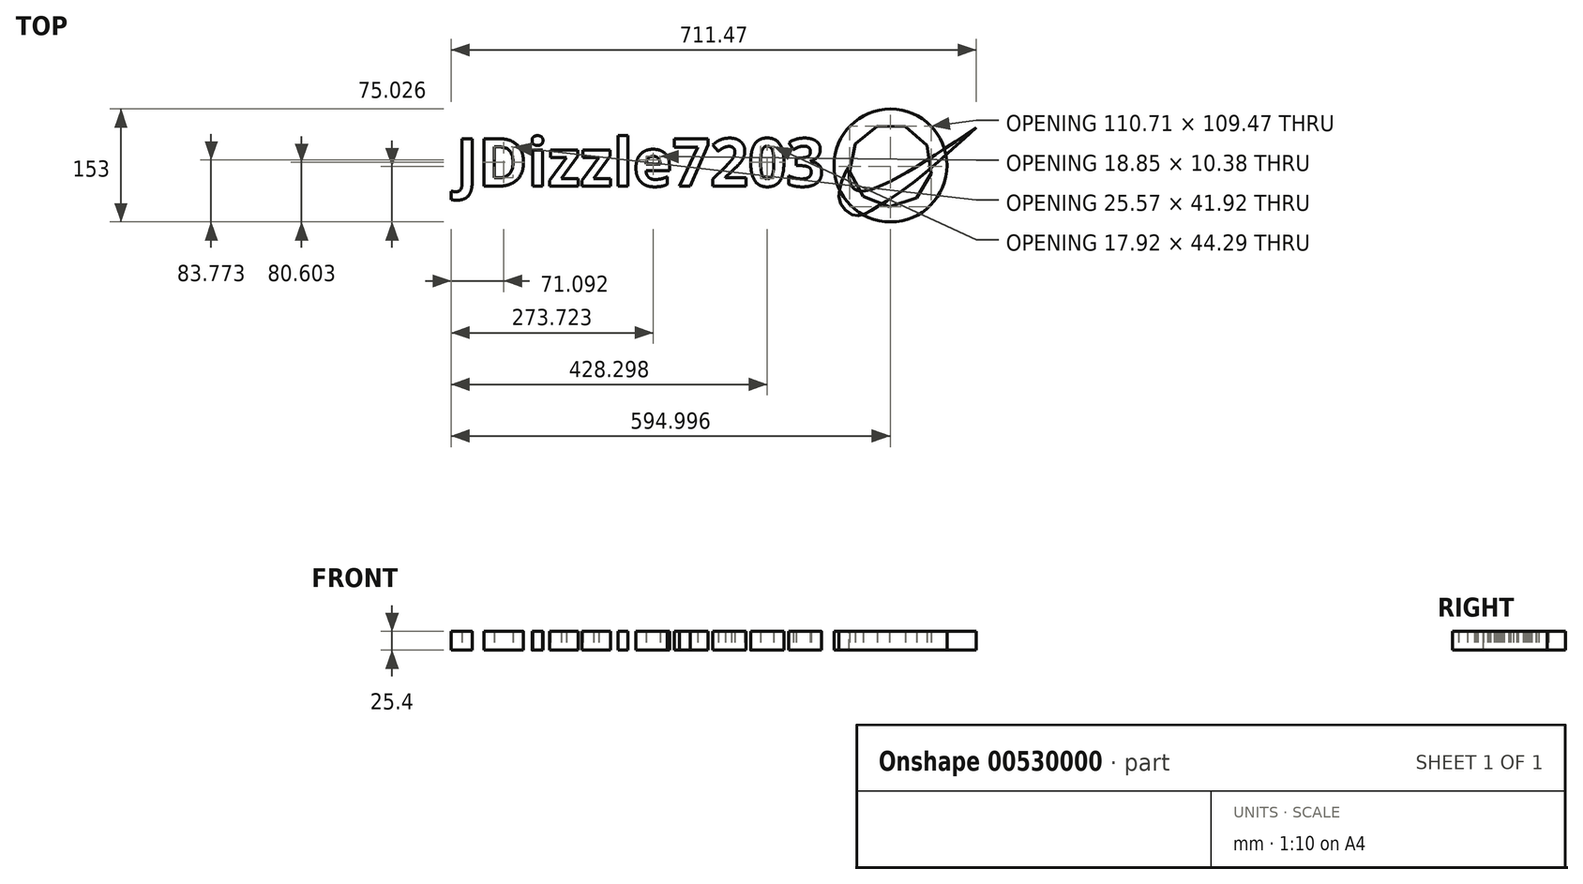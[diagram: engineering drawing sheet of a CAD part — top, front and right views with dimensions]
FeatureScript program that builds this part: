
annotation { "Feature Type Name" : "Feature", "Feature Type Description" : "" }
export const myFeature = defineFeature(function(context is Context, id is Id, definition is map)
    precondition{}
    {
        {
            var Q0;
            Q0=qCreatedBy(makeId("Top.planeOp"),FACE);
            var sketch = newSketch(context, id + "F0", { "sketchPlane" : qUnion([Q0])});
            skCircle(sketch, "E0", {"center": v(0, 0) * mm, "radius": 76.5 * mm});
            skLineSegment(sketch, "E1", {"start": v(0, 0) * mm, "end": v(56.25, -51.85) * mm});
            skLineSegment(sketch, "E2", {"start": v(56.25, -51.85) * mm, "end": v(0, 0) * mm});
            skLineSegment(sketch, "E3", {"start": v(0, 0) * mm, "end": v(48.46, 59.2) * mm});
            skLineSegment(sketch, "E4", {"start": v(48.46, 59.2) * mm, "end": v(0, 0) * mm});
            skLineSegment(sketch, "E5", {"start": v(0, 0) * mm, "end": v(-54.78, -53.4) * mm});
            skLineSegment(sketch, "E6", {"start": v(-54.78, -53.4) * mm, "end": v(0, 0) * mm});
            skLineSegment(sketch, "E7", {"start": v(0, 0) * mm, "end": v(-56.26, 51.84) * mm});
            skLineSegment(sketch, "E8", {"start": v(-56.26, 51.84) * mm, "end": v(0, 0) * mm});
            skCircle(sketch, "E9.cCircle", {"center": v(0, 0) * mm, "radius": 19.5 * mm, "construction": true});
            skLineSegment(sketch, "E9.0", {"start": v(-7.1, -19.5) * mm, "end": v(-17.97, -10.38) * mm});
            skLineSegment(sketch, "E9.1", {"start": v(-17.97, -10.38) * mm, "end": v(-20.44, 3.6) * mm});
            skLineSegment(sketch, "E9.2", {"start": v(-20.44, 3.6) * mm, "end": v(-13.34, 15.9) * mm});
            skLineSegment(sketch, "E9.3", {"start": v(-13.34, 15.9) * mm, "end": v(0, 20.75) * mm});
            skLineSegment(sketch, "E9.4", {"start": v(0, 20.75) * mm, "end": v(13.34, 15.9) * mm});
            skLineSegment(sketch, "E9.5", {"start": v(13.34, 15.9) * mm, "end": v(20.44, 3.6) * mm});
            skLineSegment(sketch, "E9.6", {"start": v(20.44, 3.6) * mm, "end": v(17.97, -10.38) * mm});
            skLineSegment(sketch, "E9.7", {"start": v(17.97, -10.38) * mm, "end": v(7.1, -19.5) * mm});
            skLineSegment(sketch, "E9.8", {"start": v(7.1, -19.5) * mm, "end": v(-7.1, -19.5) * mm});
            skPoint(sketch, "E9.0.midPoint", {"position": v(-12.54, -14.94) * mm});
            skCircle(sketch, "E10.cCircle", {"center": v(0, 0) * mm, "radius": 52.83 * mm, "construction": true});
            skLineSegment(sketch, "E10.0", {"start": v(20.44, 52.38) * mm, "end": v(49.32, 26.99) * mm});
            skLineSegment(sketch, "E10.1", {"start": v(49.32, 26.99) * mm, "end": v(55.13, -11.03) * mm});
            skLineSegment(sketch, "E10.2", {"start": v(55.13, -11.03) * mm, "end": v(35.14, -43.89) * mm});
            skLineSegment(sketch, "E10.3", {"start": v(35.14, -43.89) * mm, "end": v(-1.29, -56.2) * mm});
            skLineSegment(sketch, "E10.4", {"start": v(-1.29, -56.2) * mm, "end": v(-37.12, -42.23) * mm});
            skLineSegment(sketch, "E10.5", {"start": v(-37.12, -42.23) * mm, "end": v(-55.58, -8.5) * mm});
            skLineSegment(sketch, "E10.6", {"start": v(-55.58, -8.5) * mm, "end": v(-48.03, 29.22) * mm});
            skLineSegment(sketch, "E10.7", {"start": v(-48.03, 29.22) * mm, "end": v(-18.01, 53.26) * mm});
            skLineSegment(sketch, "E10.8", {"start": v(-18.01, 53.26) * mm, "end": v(20.44, 52.38) * mm});
            skPoint(sketch, "E10.0.midPoint", {"position": v(34.88, 39.68) * mm});
            skText(sketch, "E11", { "text": "JDizzle7203", "fontName": "OpenSans-Bold.ttf"});
            const initialGuessF0  = {"E11": [-0.58853, -0.02813, 1, 0, 0.06493]};
            skSetInitialGuess(sketch, initialGuessF0);
            skSolve(sketch);
        }
        {
            var Q0;
            Q0 = qSketchRegion(id + "F0", true);
            extrude(context, id + "F1", {"entities" : qUnion([Q0]), "depth" : 25.4 * mm, "offsetDistance" : 25.4 * mm});
        }
        {
            var Q0;
            Q0=qCreatedBy(makeId("Top.planeOp"),FACE);
            var sketch = newSketch(context, id + "F2", { "sketchPlane" : qUnion([Q0])});
            skFitSpline(sketch, "E12", {"points": [v(-55.51, 0) * mm, v(-53.63, -25.76) * mm, v(-37.5, -34.9) * mm, v(116.25, 51.38) * mm], "startDerivative": vector(-6.86, -126.83) * mm, "endDerivative": vector(324.61, 217.25) * mm});
            skFitSpline(sketch, "E13", {"points": [v(-55.51, 0) * mm, v(-61.16, -10.17) * mm, v(-68.41, -29.26) * mm, v(-67.34, -52.37) * mm, v(-49.06, -67.7) * mm, v(-33.74, -65) * mm, v(-5.78, -48.6) * mm, v(18.95, -31.94) * mm, v(49.86, -7.48) * mm, v(116.25, 51.38) * mm], "startDerivative": vector(-78.1, -132.7) * mm, "endDerivative": vector(371.4, 334.83) * mm});
            skSolve(sketch);
        }
        {
            var Q0;
            Q0=makeQuery(id+"F2.imprint","IMPRINT",FACE,{"disambiguationData":[TD([[makeQuery(id+"F2.imprint","IMPRINT",EDGE,{"derivedFrom":sQuery(id+"F2.wireOp",EDGE,"E12")}),-1.0]])]});
            extrude(context, id + "F3", {"entities" : qUnion([Q0]), "depth" : 25.4 * mm, "offsetDistance" : 25.4 * mm});
        }
    });
